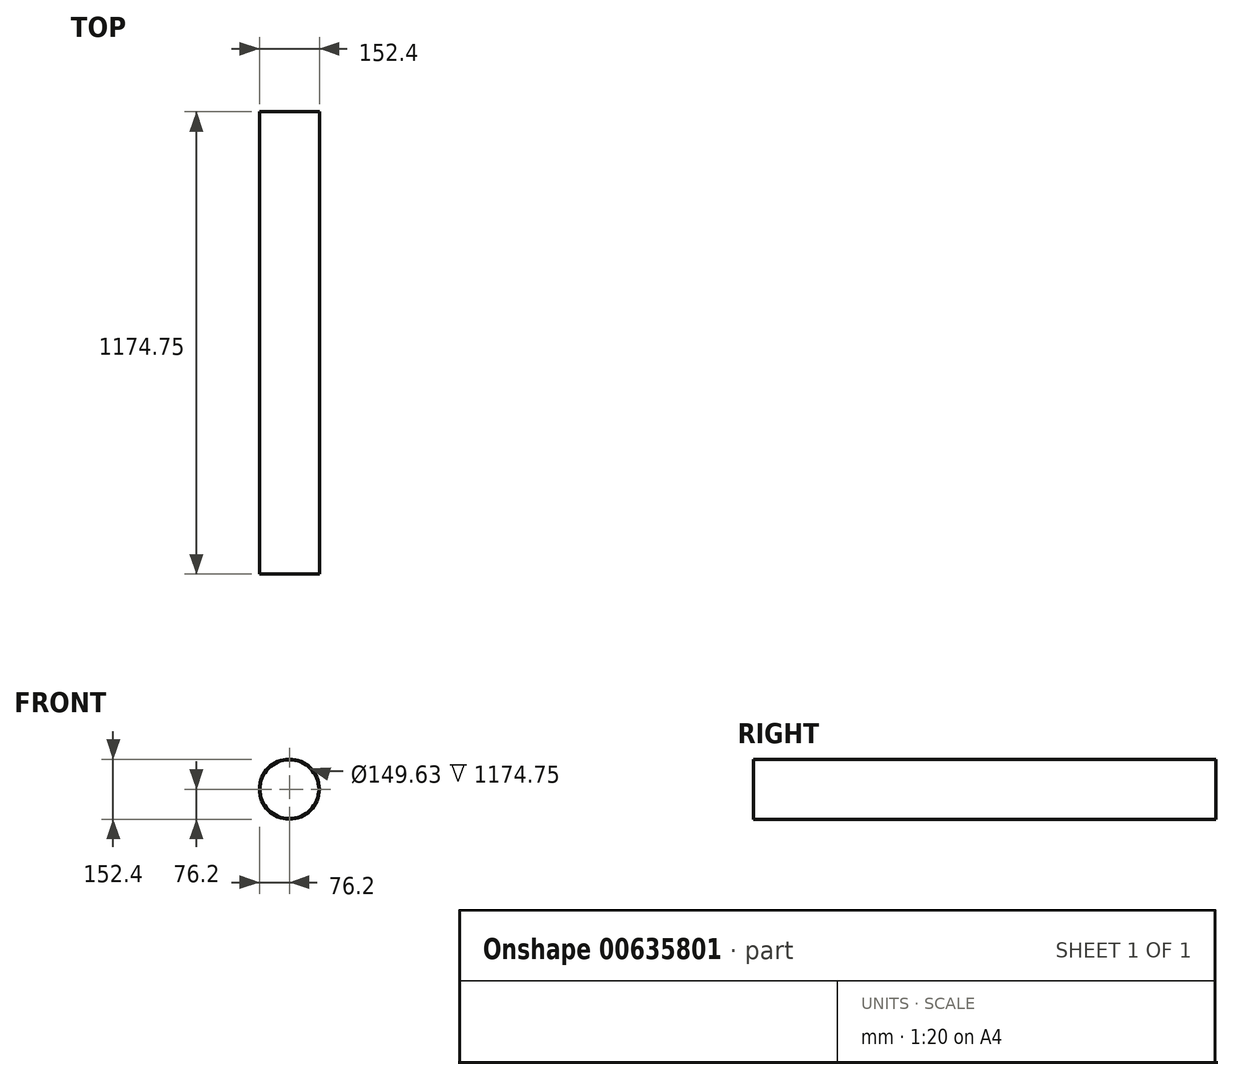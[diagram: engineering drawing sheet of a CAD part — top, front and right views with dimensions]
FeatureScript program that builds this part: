
annotation { "Feature Type Name" : "Feature", "Feature Type Description" : "" }
export const myFeature = defineFeature(function(context is Context, id is Id, definition is map)
    precondition{}
    {
        {
            var Q0;
            Q0=qCreatedBy(makeId("Front.planeOp"),FACE);
            var sketch = newSketch(context, id + "F0", { "sketchPlane" : qUnion([Q0])});
            skCircle(sketch, "E0", {"center": v(0, 0) * mm, "radius": 76.2 * mm});
            skCircle(sketch, "E1.0", {"center": v(0, 0) * mm, "radius": 74.82 * mm});
            skSolve(sketch);
        }
        {
            var Q0;
            Q0=qSketchRegion(id+"F0",true);
            extrude(context, id + "F1", {"entities" : qUnion([Q0]), "depth" : 1174.75 * mm, "offsetDistance" : 25.4 * mm});
        }
    });
